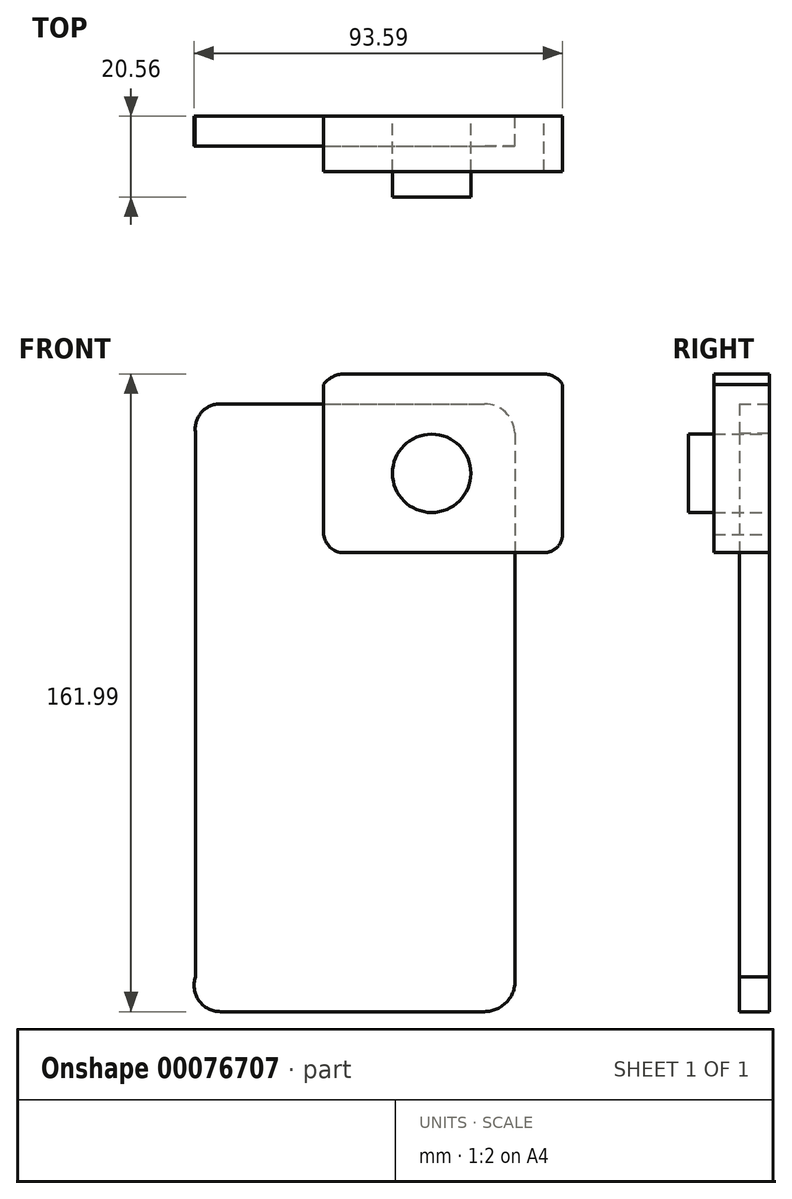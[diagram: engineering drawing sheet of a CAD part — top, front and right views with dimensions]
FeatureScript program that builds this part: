
annotation { "Feature Type Name" : "Feature", "Feature Type Description" : "" }
export const myFeature = defineFeature(function(context is Context, id is Id, definition is map)
    precondition{}
    {
        {
            var Q0;
            Q0=qCreatedBy(makeId("Front.planeOp"),FACE);
            var sketch = newSketch(context, id + "F0", { "sketchPlane" : qUnion([Q0])});
            skLineSegment(sketch, "E0", {"start": v(-47.55, 73.63) * mm, "end": v(19.5, 73.63) * mm});
            skLineSegment(sketch, "E1", {"start": v(-53.88, 66.24) * mm, "end": v(-53.88, -71.93) * mm});
            skLineSegment(sketch, "E2", {"start": v(27.24, 66.24) * mm, "end": v(27.24, -71.93) * mm});
            skLineSegment(sketch, "E3", {"start": v(-47.55, -80.8) * mm, "end": v(19.5, -80.8) * mm});
            skArc(sketch, "E4", {"start": v(-47.55, 73.63) * mm, "mid": v(-52.41, 71.4) * mm, "end": v(-53.88, 66.24) * mm});
            skArc(sketch, "E5", {"start": v(27.24, 66.24) * mm, "mid": v(24.85, 71.49) * mm, "end": v(19.5, 73.63) * mm});
            skArc(sketch, "E6", {"start": v(-53.88, -71.93) * mm, "mid": v(-53, -78) * mm, "end": v(-47.55, -80.8) * mm});
            skArc(sketch, "E7", {"start": v(19.5, -80.8) * mm, "mid": v(25.39, -78.12) * mm, "end": v(27.24, -71.93) * mm});
            skSolve(sketch);
        }
        {
            var Q0;
            Q0=makeQuery(id+"F0.imprint","IMPRINT",FACE,{"disambiguationData":[TD([[makeQuery(id+"F0.imprint","IMPRINT",EDGE,{"derivedFrom":sQuery(id+"F0.wireOp",EDGE,"E0")}),-1.0]])]});
            extrude(context, id + "F1", {"entities" : qUnion([Q0]), "depth" : 7.62 * mm});
        }
        {
            var Q0;
            Q0=qCreatedBy(makeId("Front.planeOp"),FACE);
            var sketch = newSketch(context, id + "F2", { "sketchPlane" : qUnion([Q0])});
            skLineSegment(sketch, "E8", {"start": v(34.6, 35.82) * mm, "end": v(-16.2, 35.82) * mm});
            skLineSegment(sketch, "E9", {"start": v(39.35, 40.46) * mm, "end": v(39.35, 78.56) * mm});
            skLineSegment(sketch, "E10", {"start": v(34.6, 81.19) * mm, "end": v(-16.2, 81.19) * mm});
            skLineSegment(sketch, "E11", {"start": v(-21.3, 78.56) * mm, "end": v(-21.3, 40.46) * mm});
            skArc(sketch, "E12", {"start": v(39.35, 78.56) * mm, "mid": v(37.31, 80.49) * mm, "end": v(34.6, 81.19) * mm});
            skArc(sketch, "E13", {"start": v(-16.2, 81.19) * mm, "mid": v(-19.07, 80.5) * mm, "end": v(-21.3, 78.56) * mm});
            skArc(sketch, "E14", {"start": v(34.6, 35.82) * mm, "mid": v(37.95, 37.14) * mm, "end": v(39.35, 40.46) * mm});
            skArc(sketch, "E15", {"start": v(-21.3, 40.46) * mm, "mid": v(-19.65, 37.15) * mm, "end": v(-16.2, 35.82) * mm});
            skSolve(sketch);
        }
        {
            var Q0;
            Q0=makeQuery(id+"F2.imprint","IMPRINT",FACE,{"disambiguationData":[TD([[makeQuery(id+"F2.imprint","IMPRINT",EDGE,{"derivedFrom":sQuery(id+"F2.wireOp",EDGE,"E8")}),-1.0]])]});
            var sketch = newSketch(context, id + "F3", { "sketchPlane" : qUnion([Q0])});
            skCircle(sketch, "E16", {"center": v(6.12, 55.99) * mm, "radius": 9.96 * mm});
            skSolve(sketch);
        }
        {
            var Q0;
            Q0=qSketchRegion(id+"F2",true);
            extrude(context, id + "F4", {"entities" : qUnion([Q0]), "depth" : 14.1 * mm});
        }
        {
            var Q0;
            Q0=qSketchRegion(id+"F3",true);
            extrude(context, id + "F5", {"entities" : qUnion([Q0]), "depth" : 20.56 * mm});
        }
    });
